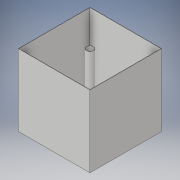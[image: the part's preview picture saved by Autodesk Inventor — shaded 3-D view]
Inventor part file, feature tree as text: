
AUTODESK INVENTOR PART (.ipt)
format: ipt  version: 2019.1 (Build 231200000, 200)  size: 116,736 bytes
history: native  units: mm
features: extrude x3, sketch x3, other x1, projected_geometry x1
ambient origin geometry x8: Origin, YZ Plane, XZ Plane, XY Plane, X Axis, Y Axis, Z Axis, Center Point
bodies: Body1 (feature_tree)
feature tree (8):
  other  "ソリッド1"
  extrude  "押し出し1"  Depth=1010.0mm
  extrude  "押し出し2"  Depth=1010.0mm
  extrude  "押し出し3"  Depth=10.0mm TaperAngle=0.0deg
  sketch  "スケッチ1"
  sketch  "スケッチ2"
  projected_geometry  "投影ループ1"
  sketch  "スケッチ3"
